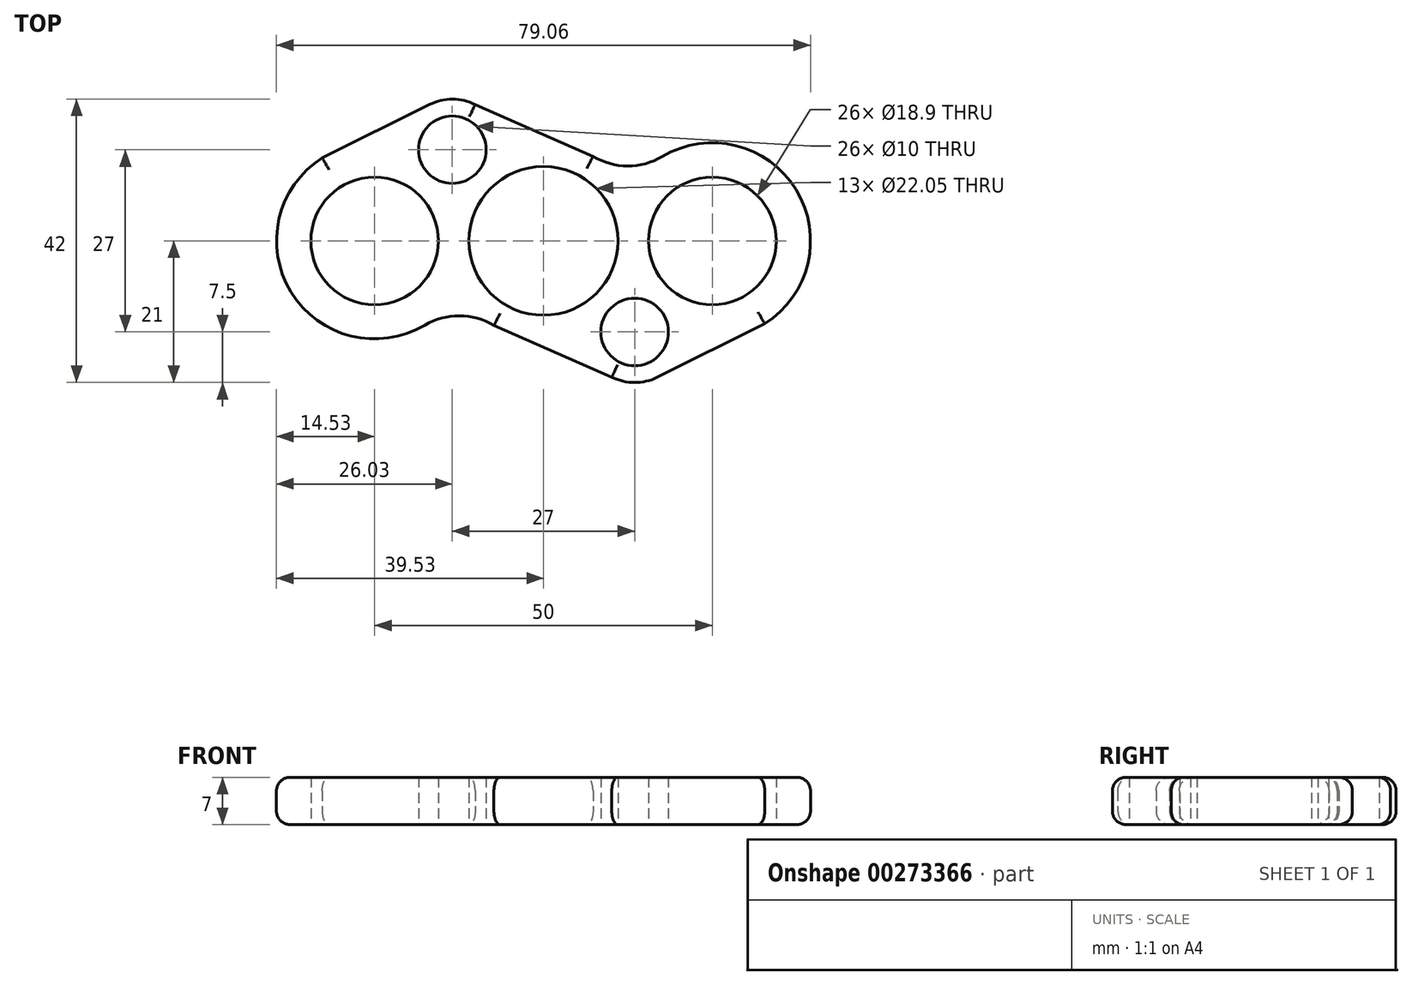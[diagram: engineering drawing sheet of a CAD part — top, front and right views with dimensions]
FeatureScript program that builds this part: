
annotation { "Feature Type Name" : "Feature", "Feature Type Description" : "" }
export const myFeature = defineFeature(function(context is Context, id is Id, definition is map)
    precondition{}
    {
        {
            var Q0;
            Q0=qCreatedBy(makeId("Top.planeOp"),FACE);
            var sketch = newSketch(context, id + "F0", { "sketchPlane" : qUnion([Q0])});
            skCircle(sketch, "E0", {"center": v(0, 0) * mm, "radius": 11.03 * mm});
            skCircle(sketch, "E1", {"center": v(-25, 0) * mm, "radius": 9.45 * mm});
            skCircle(sketch, "E2.MirrorC", {"center": v(25, 0) * mm, "radius": 9.45 * mm});
            skLineSegment(sketch, "E3", {"start": v(0, 0) * mm, "end": v(25, 0) * mm, "construction": true});
            skPoint(sketch, "E4.startSnap0", {"position": v(12.5, 0) * mm});
            skCircle(sketch, "E5", {"center": v(-25, 0) * mm, "radius": 12.5 * mm, "construction": true});
            skPoint(sketch, "E6.orphan", {"position": v(-12, -24.13) * mm});
            skPoint(sketch, "E7.orphan", {"position": v(33.68, -11.5) * mm});
            skArc(sketch, "E8", {"start": v(-32.76, 12.3) * mm, "mid": v(-37.4, -7.59) * mm, "end": v(-17.58, -12.5) * mm});
            skArc(sketch, "E9.MirrorCS", {"start": v(32.76, -12.3) * mm, "mid": v(37.4, 7.59) * mm, "end": v(17.58, 12.5) * mm});
            skPoint(sketch, "E10.visualSharp", {"position": v(12, -24.13) * mm});
            skArc(sketch, "E11.filletArc", {"start": v(7.34, 12.52) * mm, "mid": v(12.46, 11.1) * mm, "end": v(17.58, 12.5) * mm});
            skPoint(sketch, "E12.visualSharp", {"position": v(-13.47, -8.85) * mm});
            skArc(sketch, "E12.filletArc", {"start": v(-7.34, -12.52) * mm, "mid": v(-12.46, -11.1) * mm, "end": v(-17.58, -12.5) * mm});
            skCircle(sketch, "E13", {"center": v(13.5, -13.5) * mm, "radius": 5 * mm});
            skArc(sketch, "E14", {"start": v(10.12, -20.2) * mm, "mid": v(13.48, -21) * mm, "end": v(16.84, -20.21) * mm});
            skLineSegment(sketch, "E15", {"start": v(32.76, -12.3) * mm, "end": v(16.84, -20.21) * mm});
            skLineSegment(sketch, "E16", {"start": v(-7.34, -12.52) * mm, "end": v(10.12, -20.2) * mm});
            skLineSegment(sketch, "E17.MirrorCS", {"start": v(-32.76, 12.3) * mm, "end": v(-16.84, 20.21) * mm});
            skArc(sketch, "E18.MirrorCS", {"start": v(-10.12, 20.2) * mm, "mid": v(-13.48, 21) * mm, "end": v(-16.84, 20.21) * mm});
            skCircle(sketch, "E19.MirrorC", {"center": v(-13.5, 13.5) * mm, "radius": 5 * mm});
            skLineSegment(sketch, "E20.MirrorCS", {"start": v(7.34, 12.52) * mm, "end": v(-10.12, 20.2) * mm});
            skSolve(sketch);
        }
        {
            var Q0;
            Q0=makeQuery(id+"F0.imprint","IMPRINT",FACE,{"disambiguationData":[TD([[makeQuery(id+"F0.imprint","IMPRINT",EDGE,{"derivedFrom":sQuery(id+"F0.wireOp",EDGE,"E0")}),-1.0]])]});
            extrude(context, id + "F1", {"entities" : qUnion([Q0]), "depth" : 7 * mm});
        }
        {
            var Q0;
            Q0=makeQuery(id+"F1.opExtrude","CAP_EDGE",EDGE,{"disambiguationData":[OSD([sQuery(id+"F0.wireOp",EDGE,"E8")])],"isStart":false});
            var Q1;
            Q1=makeQuery(id+"F1.opExtrude","CAP_EDGE",EDGE,{"disambiguationData":[OSD([sQuery(id+"F0.wireOp",EDGE,"E8")])],"isStart":true});
            var Q2;
            Q2=makeQuery(id+"F1.opExtrude","CAP_EDGE",EDGE,{"disambiguationData":[OSD([sQuery(id+"F0.wireOp",EDGE,"E12.filletArc")])],"isStart":true});
            var Q3;
            Q3=makeQuery(id+"F1.opExtrude","CAP_EDGE",EDGE,{"disambiguationData":[OSD([sQuery(id+"F0.wireOp",EDGE,"E12.filletArc")])],"isStart":false});
            var Q4;
            Q4=makeQuery(id+"F1.opExtrude","CAP_EDGE",EDGE,{"disambiguationData":[OSD([sQuery(id+"F0.wireOp",EDGE,"63cf9f15-4b01-4b64-b426-66387fe4bd120.MirrorCS")])],"isStart":false});
            var Q5;
            Q5=makeQuery(id+"F1.opExtrude","CAP_EDGE",EDGE,{"disambiguationData":[OSD([sQuery(id+"F0.wireOp",EDGE,"E10.filletArc")])],"isStart":true});
            var Q6;
            Q6=makeQuery(id+"F1.opExtrude","CAP_EDGE",EDGE,{"disambiguationData":[OSD([sQuery(id+"F0.wireOp",EDGE,"E10.filletArc")])],"isStart":false});
            var Q7;
            Q7=makeQuery(id+"F1.opExtrude","CAP_EDGE",EDGE,{"disambiguationData":[OSD([sQuery(id+"F0.wireOp",EDGE,"6Pe4Jvnd-ELGY-pnoM-UM4t-qtF1MqXWWsjN")])],"isStart":false});
            var Q8;
            Q8=makeQuery(id+"F1.opExtrude","CAP_EDGE",EDGE,{"disambiguationData":[OSD([sQuery(id+"F0.wireOp",EDGE,"6Pe4Jvnd-ELGY-pnoM-UM4t-qtF1MqXWWsjN")])],"isStart":true});
            var Q9;
            Q9=makeQuery(id+"F1.opExtrude","CAP_EDGE",EDGE,{"disambiguationData":[OSD([sQuery(id+"F0.wireOp",EDGE,"E9.MirrorCS")])],"isStart":false});
            var Q10;
            Q10=makeQuery(id+"F1.opExtrude","CAP_EDGE",EDGE,{"disambiguationData":[OSD([sQuery(id+"F0.wireOp",EDGE,"E9.MirrorCS")])],"isStart":true});
            var Q11;
            Q11=makeQuery(id+"F1.opExtrude","CAP_EDGE",EDGE,{"disambiguationData":[OSD([sQuery(id+"F0.wireOp",EDGE,"63cf9f15-4b01-4b64-b426-66387fe4bd120.MirrorCS")])],"isStart":true});
            var Q12;
            Q12=makeQuery(id+"F1.opExtrude","CAP_EDGE",EDGE,{"disambiguationData":[OSD([sQuery(id+"F0.wireOp",EDGE,"6d008dc7-4d6b-4d10-a692-438fe680b6350.MirrorCS")])],"isStart":false});
            var Q13;
            Q13=makeQuery(id+"F1.opExtrude","CAP_EDGE",EDGE,{"disambiguationData":[OSD([sQuery(id+"F0.wireOp",EDGE,"b5781efa-84cc-45d5-8bed-d61ee13e0e28.filletArc")])],"isStart":false});
            var Q14;
            Q14=makeQuery(id+"F1.opExtrude","CAP_EDGE",EDGE,{"disambiguationData":[OSD([sQuery(id+"F0.wireOp",EDGE,"K1M5tBrC-aizg-28Ey-nQP9-qzbyxEps72cR")])],"isStart":false});
            var Q15;
            Q15=makeQuery(id+"F1.opExtrude","CAP_EDGE",EDGE,{"disambiguationData":[OSD([sQuery(id+"F0.wireOp",EDGE,"E11.filletArc")])],"isStart":false});
            var Q16;
            Q16=makeQuery(id+"F1.opExtrude","CAP_EDGE",EDGE,{"disambiguationData":[OSD([sQuery(id+"F0.wireOp",EDGE,"E16")])],"isStart":false});
            var Q17;
            Q17=makeQuery(id+"F1.opExtrude","CAP_EDGE",EDGE,{"disambiguationData":[OSD([sQuery(id+"F0.wireOp",EDGE,"E14")])],"isStart":false});
            var Q18;
            Q18=makeQuery(id+"F1.opExtrude","CAP_EDGE",EDGE,{"disambiguationData":[OSD([sQuery(id+"F0.wireOp",EDGE,"E15")])],"isStart":false});
            var Q19;
            Q19=makeQuery(id+"F1.opExtrude","CAP_EDGE",EDGE,{"disambiguationData":[OSD([sQuery(id+"F0.wireOp",EDGE,"E16")])],"isStart":true});
            var Q20;
            Q20=makeQuery(id+"F1.opExtrude","CAP_EDGE",EDGE,{"disambiguationData":[OSD([sQuery(id+"F0.wireOp",EDGE,"E14")])],"isStart":true});
            var Q21;
            Q21=makeQuery(id+"F1.opExtrude","CAP_EDGE",EDGE,{"disambiguationData":[OSD([sQuery(id+"F0.wireOp",EDGE,"E15")])],"isStart":true});
            var Q22;
            Q22=makeQuery(id+"F1.opExtrude","CAP_EDGE",EDGE,{"disambiguationData":[OSD([sQuery(id+"F0.wireOp",EDGE,"E17.MirrorCS")])],"isStart":true});
            var Q23;
            Q23=makeQuery(id+"F1.opExtrude","CAP_EDGE",EDGE,{"disambiguationData":[OSD([sQuery(id+"F0.wireOp",EDGE,"E18.MirrorCS")])],"isStart":true});
            var Q24;
            Q24=makeQuery(id+"F1.opExtrude","CAP_EDGE",EDGE,{"disambiguationData":[OSD([sQuery(id+"F0.wireOp",EDGE,"E20.MirrorCS")])],"isStart":true});
            var Q25;
            Q25=makeQuery(id+"F1.opExtrude","CAP_EDGE",EDGE,{"disambiguationData":[OSD([sQuery(id+"F0.wireOp",EDGE,"E11.filletArc")])],"isStart":true});
            var Q26;
            Q26=makeQuery(id+"F1.opExtrude","CAP_EDGE",EDGE,{"disambiguationData":[OSD([sQuery(id+"F0.wireOp",EDGE,"E17.MirrorCS")])],"isStart":false});
            var Q27;
            Q27=makeQuery(id+"F1.opExtrude","CAP_EDGE",EDGE,{"disambiguationData":[OSD([sQuery(id+"F0.wireOp",EDGE,"E18.MirrorCS")])],"isStart":false});
            fillet(context, id + "F2", {"entities" : qUnion([Q0, Q1, Q2, Q3, Q4, Q5, Q6, Q7, Q8, Q9, Q10, Q11, Q12, Q13, Q14, Q15, Q16, Q17, Q18, Q19, Q20, Q21, Q22, Q23, Q24, Q25, Q26, Q27]), "radius" : 2 * mm, "tangentPropagation" : true, "allowEdgeOverflow" : false});
        }
    });
